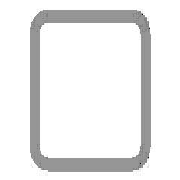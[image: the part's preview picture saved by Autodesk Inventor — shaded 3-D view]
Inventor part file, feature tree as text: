
AUTODESK INVENTOR PART (.ipt)
format: ipt  version: 2022 (Build 260153000, 153)  size: 150,528 bytes
history: native  units: mm (DEFAULTED — no unit token found)
features: other x4, sketch x3, plane x2, extrude x1, split x1
ambient origin geometry x8: Origin, YZ Plane, XZ Plane, XY Plane, X Axis, Y Axis, Z Axis, Center Point
bodies: Solid1 (feature_tree)
feature tree (11):
  parser-record x1  (decoder bookkeeping rows leaked as tree rows — omitted from the tree; the rows remain in map.json)
  other  "Driven Length"
  other  "Plano inicial"
  other  "Plano final"
  extrude  "Cuerpo"  TaperAngle=0.0deg  [1 undecoded]
  plane  "Plano de trabajo4"
  split  "Dividir1"
  sketch  "Boceto"  dims[d10=40.0mm d11=40.0mm d12=5.0mm d13=-20.0mm d14=400.0mm d15=20.0mm d16=20.0mm d17=90.0deg d18=420.0mm]
  sketch  "Sketch3"  dims[d3=420.0mm d4=0.0mm]
  plane  "Work Plane3"
  sketch  "Sketch4"  dims[d7=7.5mm]
note: 1 required parameter value undecoded (feature->parameter linkage not recoverable at this tier; creation-order binding heuristic only, values carry confidence <= 0.55)
